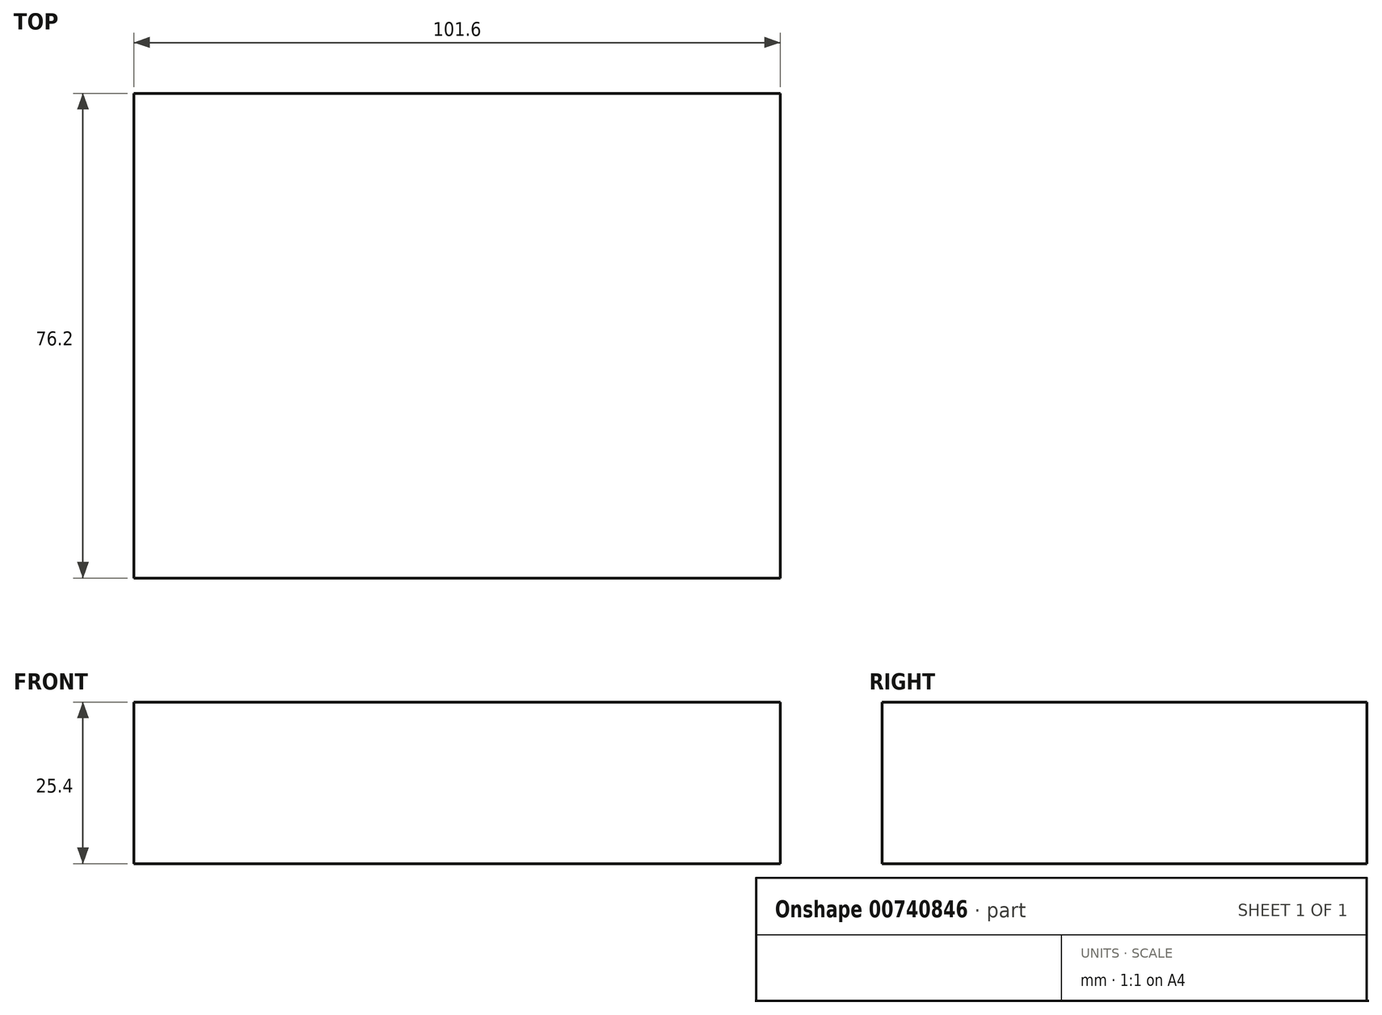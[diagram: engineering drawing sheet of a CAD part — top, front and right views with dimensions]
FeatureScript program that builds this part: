
annotation { "Feature Type Name" : "Feature", "Feature Type Description" : "" }
export const myFeature = defineFeature(function(context is Context, id is Id, definition is map)
    precondition{}
    {
        {
            var Q0;
            Q0=qCreatedBy(makeId("Front.planeOp"),FACE);
            var sketch = newSketch(context, id + "F0", { "sketchPlane" : qUnion([Q0])});
            skLineSegment(sketch, "E0.bottom", {"start": v(50.8, 12.7) * mm, "end": v(-50.8, 12.7) * mm});
            skLineSegment(sketch, "E0.top", {"start": v(50.8, -12.7) * mm, "end": v(-50.8, -12.7) * mm});
            skLineSegment(sketch, "E0.left", {"start": v(50.8, 12.7) * mm, "end": v(50.8, -12.7) * mm});
            skLineSegment(sketch, "E0.right", {"start": v(-50.8, 12.7) * mm, "end": v(-50.8, -12.7) * mm});
            skPoint(sketch, "E0.middle", {"position": v(0, 0) * mm});
            skSolve(sketch);
        }
        {
            var Q0;
            Q0 = qSketchRegion(id + "F0", true);
            extrude(context, id + "F1", {"entities" : qUnion([Q0]), "depth" : 76.2 * mm, "offsetDistance" : 25.4 * mm});
        }
    });
